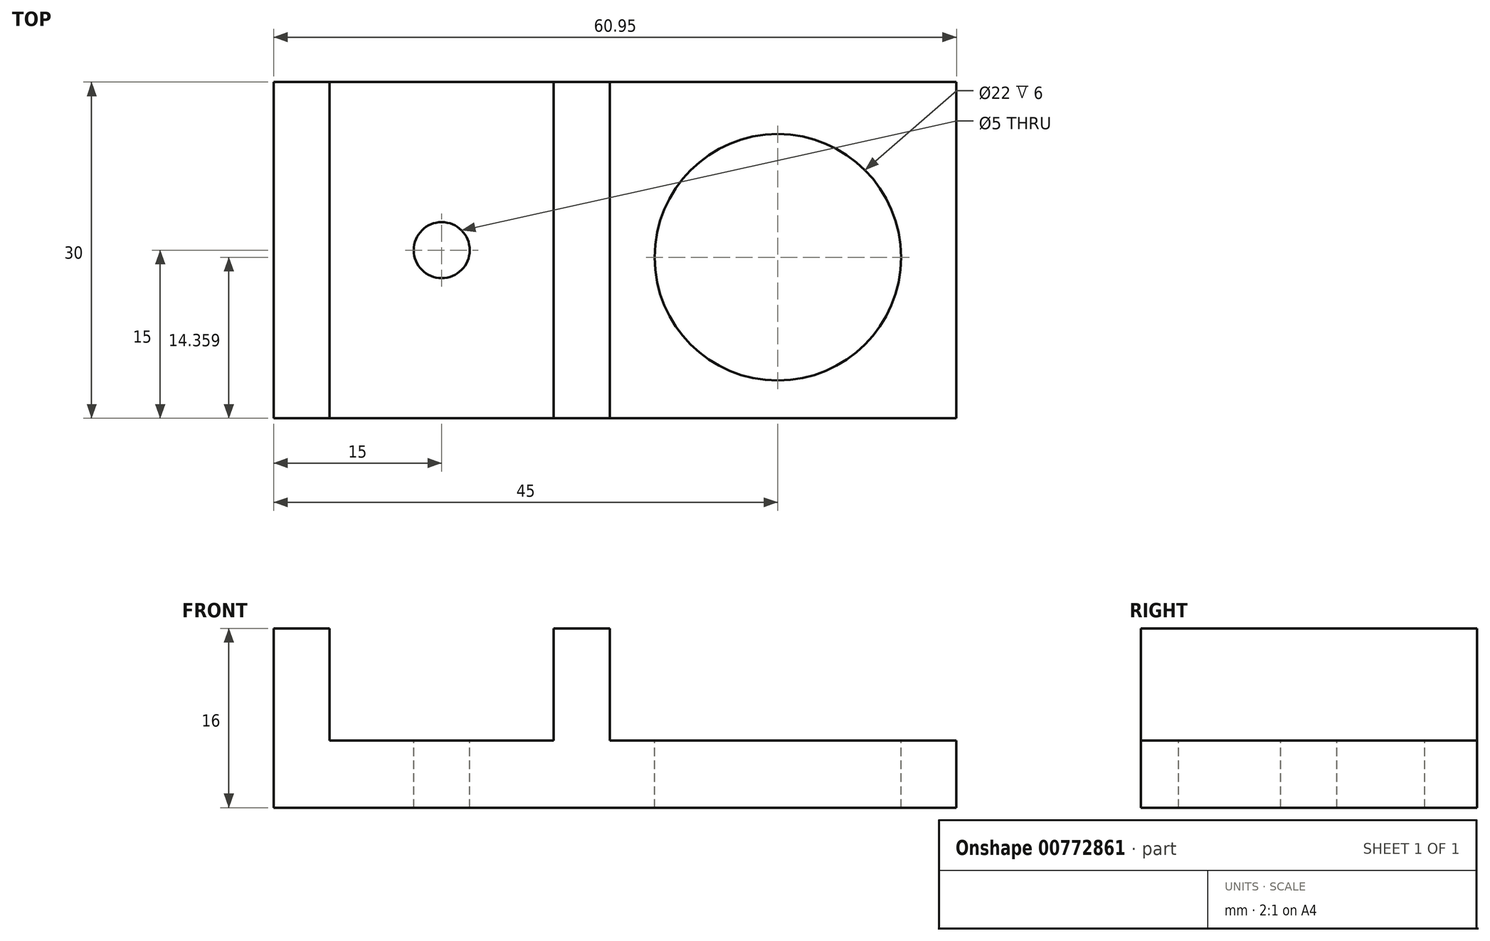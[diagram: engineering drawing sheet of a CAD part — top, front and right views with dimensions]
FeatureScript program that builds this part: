
annotation { "Feature Type Name" : "Feature", "Feature Type Description" : "" }
export const myFeature = defineFeature(function(context is Context, id is Id, definition is map)
    precondition{}
    {
        {
            var Q0;
            Q0=qCreatedBy(makeId("Front.planeOp"),FACE);
            var sketch = newSketch(context, id + "F0", { "sketchPlane" : qUnion([Q0])});
            skLineSegment(sketch, "E0.bottom", {"start": v(-35.72, 10.1) * mm, "end": v(25.23, 10.1) * mm});
            skLineSegment(sketch, "E0.top", {"start": v(-35.72, 4.1) * mm, "end": v(25.23, 4.1) * mm});
            skLineSegment(sketch, "E0.left", {"start": v(-35.72, 10.1) * mm, "end": v(-35.72, 4.1) * mm});
            skLineSegment(sketch, "E0.right", {"start": v(25.23, 10.1) * mm, "end": v(25.23, 4.1) * mm});
            skLineSegment(sketch, "E1.bottom", {"start": v(-35.72, 10.1) * mm, "end": v(-30.72, 10.1) * mm});
            skLineSegment(sketch, "E1.top", {"start": v(-35.72, 20.1) * mm, "end": v(-30.72, 20.1) * mm});
            skLineSegment(sketch, "E1.left", {"start": v(-35.72, 10.1) * mm, "end": v(-35.72, 20.1) * mm});
            skLineSegment(sketch, "E1.right", {"start": v(-30.72, 10.1) * mm, "end": v(-30.72, 20.1) * mm});
            skLineSegment(sketch, "E2.bottom", {"start": v(-10.72, 10.1) * mm, "end": v(-5.72, 10.1) * mm});
            skLineSegment(sketch, "E2.top", {"start": v(-10.72, 20.1) * mm, "end": v(-5.72, 20.1) * mm});
            skLineSegment(sketch, "E2.left", {"start": v(-10.72, 10.1) * mm, "end": v(-10.72, 20.1) * mm});
            skLineSegment(sketch, "E2.right", {"start": v(-5.72, 10.1) * mm, "end": v(-5.72, 20.1) * mm});
            skPoint(sketch, "E3", {"position": v(-20.72, 10.1) * mm});
            skPoint(sketch, "E4", {"position": v(9.28, 10.1) * mm});
            skSolve(sketch);
        }
        {
            var Q0;
            Q0 = qSketchRegion(id + "F0", true);
            var Q1;
            Q1 = qSketchRegion(id + "F2", true);
            extrude(context, id + "F1", {"entities" : qUnion([Q0, Q1]), "depth" : 30 * mm, "offsetDistance" : 25 * mm});
        }
        {
            var Q0;
            {var subQ0=sQuery(id+"F0.wireOp",EDGE,"E0.bottom");Q0=makeQuery(id+"F1.opExtrude","SWEPT_FACE",FACE,{"disambiguationData":[OSD([subQ0]),TDD([makeQuery(id+"F0.imprint","IMPRINT",EDGE,{"disambiguationData":[TD([[makeQuery(id+"F0.imprint","INTERSECT",VERTEX,{"derivedFrom":[subQ0,sQuery(id+"F0.wireOp",EDGE,"E0.right")]}),1.0]])],"derivedFrom":subQ0})])]});}
            var sketch = newSketch(context, id + "F2", { "sketchPlane" : qUnion([Q0])});
            skCircle(sketch, "E5", {"center": v(9.28, -15.64) * mm, "radius": 11 * mm});
            skCircle(sketch, "E6", {"center": v(-20.72, -15) * mm, "radius": 2.5 * mm});
            skSolve(sketch);
        }
        {
            var Q0;
            Q0=sQuery(id+"F2.wireOp",VERTEX,"E5.center");
            var Q1;
            Q1=makeQuery(id+"F1.opExtrude","SWEPT_BODY",BODY,{"disambiguationData":[OSD([sQuery(id+"F0.wireOp",EDGE,"E0.bottom"),sQuery(id+"F0.wireOp",EDGE,"E0.top"),sQuery(id+"F0.wireOp",EDGE,"E0.left"),sQuery(id+"F0.wireOp",EDGE,"E0.right"),sQuery(id+"F0.wireOp",EDGE,"E1.top"),sQuery(id+"F0.wireOp",EDGE,"E1.left"),sQuery(id+"F0.wireOp",EDGE,"E1.right"),sQuery(id+"F0.wireOp",EDGE,"E2.top"),sQuery(id+"F0.wireOp",EDGE,"E2.left"),sQuery(id+"F0.wireOp",EDGE,"E2.right")])]});
            hole(context, id + "F3", {"style" : HoleStyle.SIMPLE, "endStyle" : HoleEndStyle.THROUGH, "holeDiameter" : 22 * mm, "majorDiameter" : 5 * mm, "isTappedThrough" : true, "tappedDepth" : 12 * mm, "tapClearance" : 3, "locations" : qUnion([Q0]), "scope" : qUnion([Q1])});
        }
        {
            var Q0;
            {var subQ0=sQuery(id+"F0.wireOp",EDGE,"E0.bottom");Q0=makeQuery(id+"F1.opExtrude","SWEPT_FACE",FACE,{"disambiguationData":[OSD([subQ0]),TDD([makeQuery(id+"F0.imprint","IMPRINT",EDGE,{"disambiguationData":[TD([[makeQuery(id+"F0.imprint","INTERSECT",VERTEX,{"derivedFrom":[subQ0,sQuery(id+"F0.wireOp",EDGE,"E1.bottom"),sQuery(id+"F0.wireOp",EDGE,"E1.right")]}),-1.0]])],"derivedFrom":subQ0})])]});}
            var sketch = newSketch(context, id + "F4", { "sketchPlane" : qUnion([Q0])});
            skCircle(sketch, "E7", {"center": v(-20.72, -15) * mm, "radius": 2.5 * mm});
            skSolve(sketch);
        }
        {
            var Q0;
            Q0=sQuery(id+"F4.wireOp",VERTEX,"E7.center");
            var Q1;
            Q1=makeQuery(id+"F1.opExtrude","SWEPT_BODY",BODY,{"disambiguationData":[OSD([sQuery(id+"F0.wireOp",EDGE,"E0.bottom"),sQuery(id+"F0.wireOp",EDGE,"E0.top"),sQuery(id+"F0.wireOp",EDGE,"E0.left"),sQuery(id+"F0.wireOp",EDGE,"E0.right"),sQuery(id+"F0.wireOp",EDGE,"E1.top"),sQuery(id+"F0.wireOp",EDGE,"E1.left"),sQuery(id+"F0.wireOp",EDGE,"E1.right"),sQuery(id+"F0.wireOp",EDGE,"E2.top"),sQuery(id+"F0.wireOp",EDGE,"E2.left"),sQuery(id+"F0.wireOp",EDGE,"E2.right")])]});
            hole(context, id + "F5", {"style" : HoleStyle.SIMPLE, "endStyle" : HoleEndStyle.THROUGH, "holeDiameter" : 5 * mm, "majorDiameter" : 5 * mm, "isTappedThrough" : true, "tappedDepth" : 12 * mm, "tapClearance" : 3, "locations" : qUnion([Q0]), "scope" : qUnion([Q1])});
        }
    });
